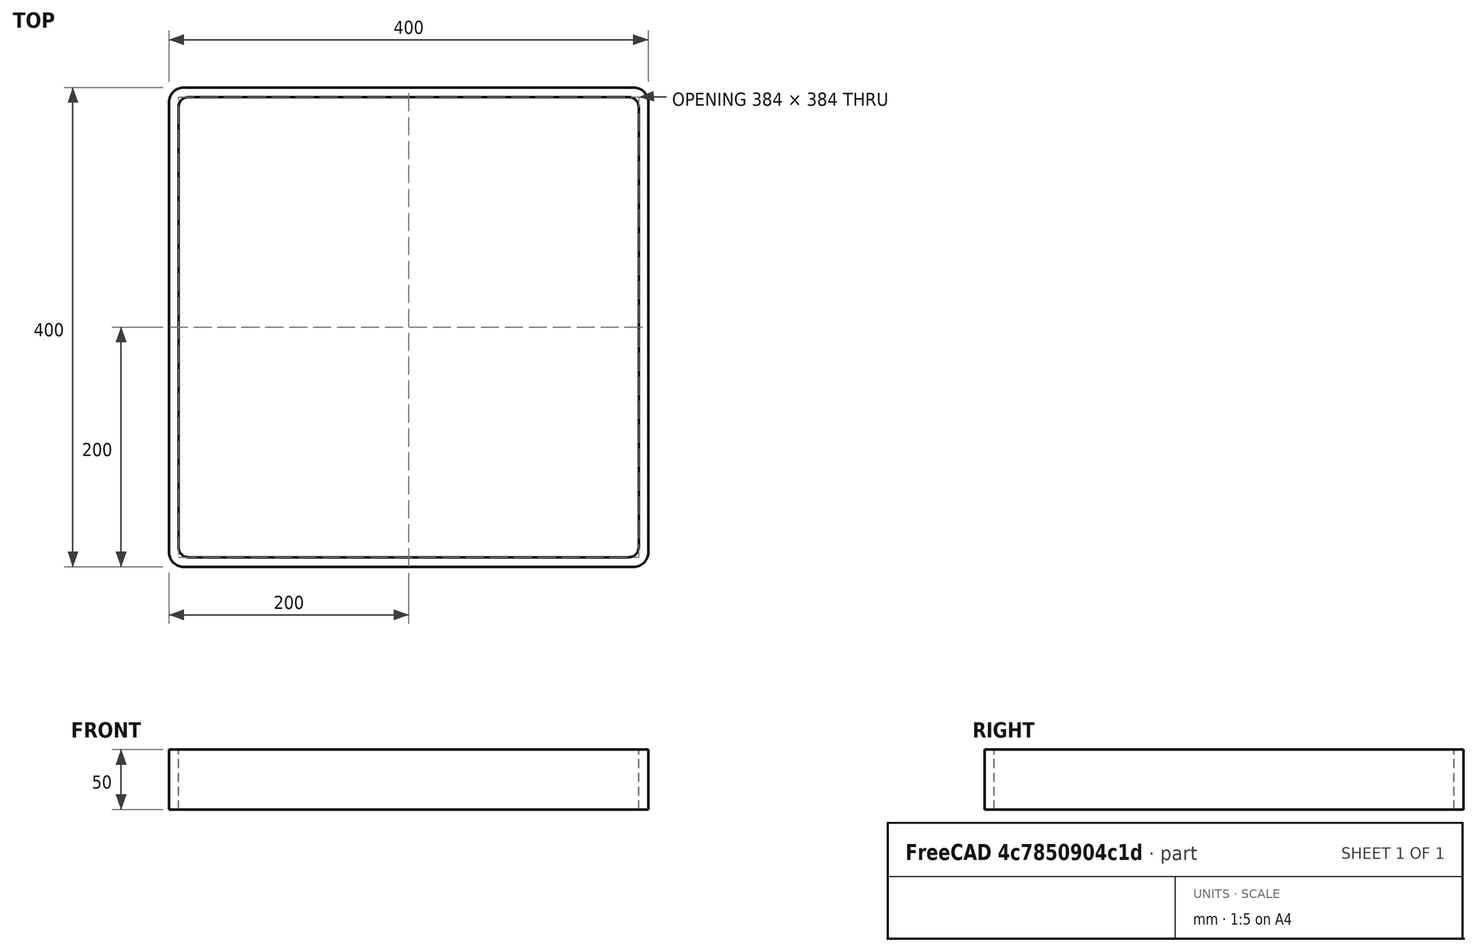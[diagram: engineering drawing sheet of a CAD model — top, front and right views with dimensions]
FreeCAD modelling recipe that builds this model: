
FCSTD DOCUMENT  (FreeCAD 0.15R4671 (Git))
Label: Square hollow section 400x400x8 EN10219 S235JRH
License: All rights reserved
LicenseURL: http://en.wikipedia.org/wiki/All_rights_reserved
objects: Sketcher::SketchObject×1, Part::Extrusion×1
note: 2 computed .brp shape members not serialized (recipe doc carries the construction recipe); baked Part::Feature solids carry a one-line shape summary decoded from their .brp

FEATURE [Sketcher::SketchObject] Sketch
  sketch-geometry (16):
    g0: LineSegment StartX=-184 StartY=192 StartZ=0 EndX=184 EndY=192 EndZ=0
    g1: LineSegment StartX=192 StartY=184 StartZ=0 EndX=192 EndY=-184 EndZ=0
    g2: LineSegment StartX=184 StartY=-192 StartZ=0 EndX=-184 EndY=-192 EndZ=0
    g3: LineSegment StartX=-192 StartY=-184 StartZ=0 EndX=-192 EndY=184 EndZ=0
    g4: LineSegment StartX=-188 StartY=200 StartZ=0 EndX=188 EndY=200 EndZ=0
    g5: LineSegment StartX=200 StartY=188 StartZ=0 EndX=200 EndY=-188 EndZ=0
    g6: LineSegment StartX=188 StartY=-200 StartZ=0 EndX=-188 EndY=-200 EndZ=0
    g7: LineSegment StartX=-200 StartY=-188 StartZ=0 EndX=-200 EndY=188 EndZ=0
    g8: ArcOfCircle CenterX=-184 CenterY=184 CenterZ=0 NormalX=0 NormalY=0 NormalZ=1 Radius=8 StartAngle=1.5708 EndAngle=3.14159
    g9: ArcOfCircle CenterX=184 CenterY=184 CenterZ=0 NormalX=0 NormalY=0 NormalZ=1 Radius=8 StartAngle=0 EndAngle=1.5708
    g10: ArcOfCircle CenterX=184 CenterY=-184 CenterZ=0 NormalX=0 NormalY=0 NormalZ=1 Radius=8 StartAngle=4.71239 EndAngle=6.28319
    g11: ArcOfCircle CenterX=-184 CenterY=-184 CenterZ=0 NormalX=0 NormalY=0 NormalZ=1 Radius=8 StartAngle=3.14159 EndAngle=4.71239
    g12: ArcOfCircle CenterX=188 CenterY=188 CenterZ=0 NormalX=0 NormalY=0 NormalZ=1 Radius=12 StartAngle=0 EndAngle=1.5708
    g13: ArcOfCircle CenterX=188 CenterY=-188 CenterZ=0 NormalX=0 NormalY=0 NormalZ=1 Radius=12 StartAngle=4.71239 EndAngle=6.28319
    g14: ArcOfCircle CenterX=-188 CenterY=-188 CenterZ=0 NormalX=0 NormalY=0 NormalZ=1 Radius=12 StartAngle=3.14159 EndAngle=4.71239
    g15: ArcOfCircle CenterX=-188 CenterY=188 CenterZ=0 NormalX=0 NormalY=0 NormalZ=1 Radius=12 StartAngle=1.5708 EndAngle=3.14159
  constraints (36):
    c: Horizontal(g2)
    c: Vertical(g3)
    c: Horizontal(g6)
    c: Vertical(g7)
    c: Tangent(g3,g8) = 1.5708
    c: Tangent(g0,g8) = 1.5708
    c: Tangent(g0,g9) = 1.5708
    c: Tangent(g1,g9) = 1.5708
    c: Tangent(g1,g10) = 1.5708
    c: Tangent(g2,g10) = 1.5708
    c: Tangent(g2,g11) = 1.5708
    c: Tangent(g3,g11) = 1.5708
    c: Tangent(g4,g12) = 1.5708
    c: Tangent(g5,g12) = 1.5708
    c: Tangent(g5,g13) = 1.5708
    c: Tangent(g6,g13) = 1.5708
    c: Tangent(g6,g14) = 1.5708
    c: Tangent(g7,g14) = 1.5708
    c: Tangent(g7,g15) = 1.5708
    c: Tangent(g4,g15) = 1.5708
    c: Equal(g9,g8)
    c: Equal(g9,g11)
    c: Equal(g9,g10)
    c: Equal(g12,g15)
    c: Equal(g12,g14)
    c: Equal(g12,g13)
    c: Symmetric(g4,g6,g-1)
    c: Symmetric(g7,g5,g-2)
    c: DistanceY(g4,g6) = -400
    c: DistanceX(g7,g5) = 400
    c: Symmetric(g3,g1,g-2)
    c: Symmetric(g0,g2,g-1)
    c: DistanceY(g0,g4) = 8
    c: DistanceX(g5,g1) = -8
    c: Radius(g9) = 8
    c: Radius(g12) = 12
FEATURE [Part::Extrusion] Extrude  label="Square hollow section 400x400x8 EN10219 S235JRH"
  Base = -> Sketch
  Dir = (0,0,50)
  Solid = true
